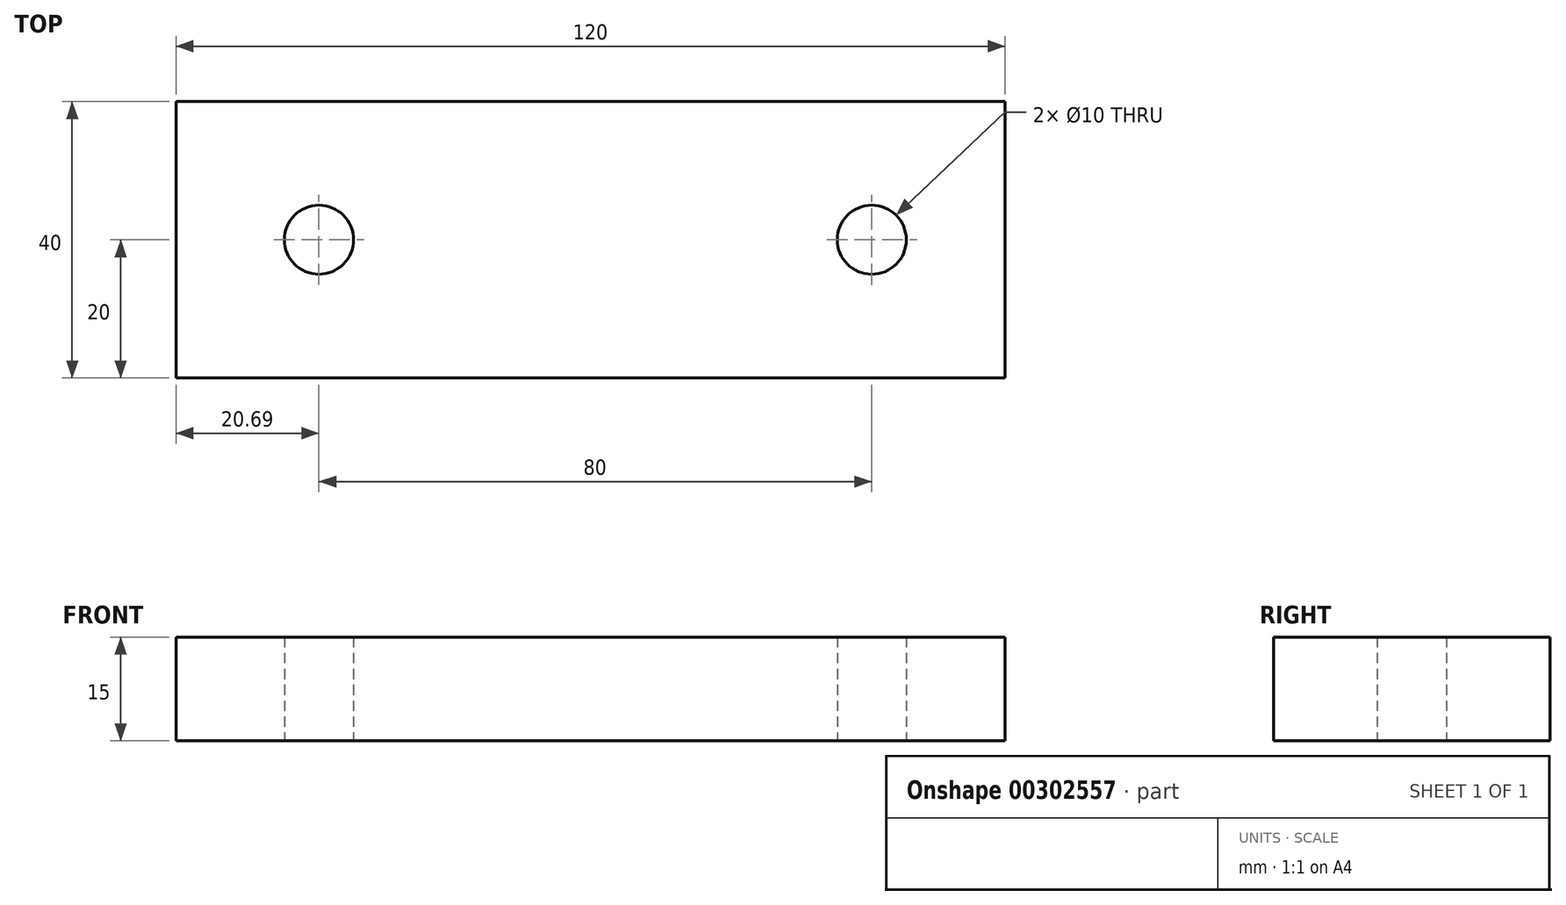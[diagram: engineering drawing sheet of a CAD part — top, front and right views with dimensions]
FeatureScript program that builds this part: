
annotation { "Feature Type Name" : "Feature", "Feature Type Description" : "" }
export const myFeature = defineFeature(function(context is Context, id is Id, definition is map)
    precondition{}
    {
        {
            var Q0;
            Q0=qCreatedBy(makeId("Top.planeOp"),FACE);
            var sketch = newSketch(context, id + "F0", { "sketchPlane" : qUnion([Q0])});
            skLineSegment(sketch, "E0", {"start": v(-40, 0) * mm, "end": v(40, 0) * mm, "construction": true});
            skCircle(sketch, "E1", {"center": v(-40, 0) * mm, "radius": 5 * mm});
            skCircle(sketch, "E2", {"center": v(40, 0) * mm, "radius": 5 * mm});
            skLineSegment(sketch, "E3", {"start": v(-60.7, 20) * mm, "end": v(59.3, 20) * mm});
            skLineSegment(sketch, "E4", {"start": v(59.3, 20) * mm, "end": v(59.3, -20) * mm});
            skLineSegment(sketch, "E5", {"start": v(59.3, -20) * mm, "end": v(-60.7, -20) * mm});
            skLineSegment(sketch, "E6", {"start": v(-60.7, -20) * mm, "end": v(-60.7, 20) * mm});
            skLineSegment(sketch, "E7", {"start": v(-60.7, 20) * mm, "end": v(-40, 0) * mm, "construction": true});
            skLineSegment(sketch, "E8", {"start": v(-60.7, -20) * mm, "end": v(-40, 0) * mm, "construction": true});
            skLineSegment(sketch, "E9", {"start": v(59.3, -20) * mm, "end": v(40, 0) * mm, "construction": true});
            skLineSegment(sketch, "E10", {"start": v(59.3, 20) * mm, "end": v(40, 0) * mm, "construction": true});
            skSolve(sketch);
        }
        {
            var Q0;
            Q0 = qSketchRegion(id + "F0", true);
            extrude(context, id + "F1", {"entities" : qUnion([Q0]), "depth" : 15 * mm});
        }
    });
